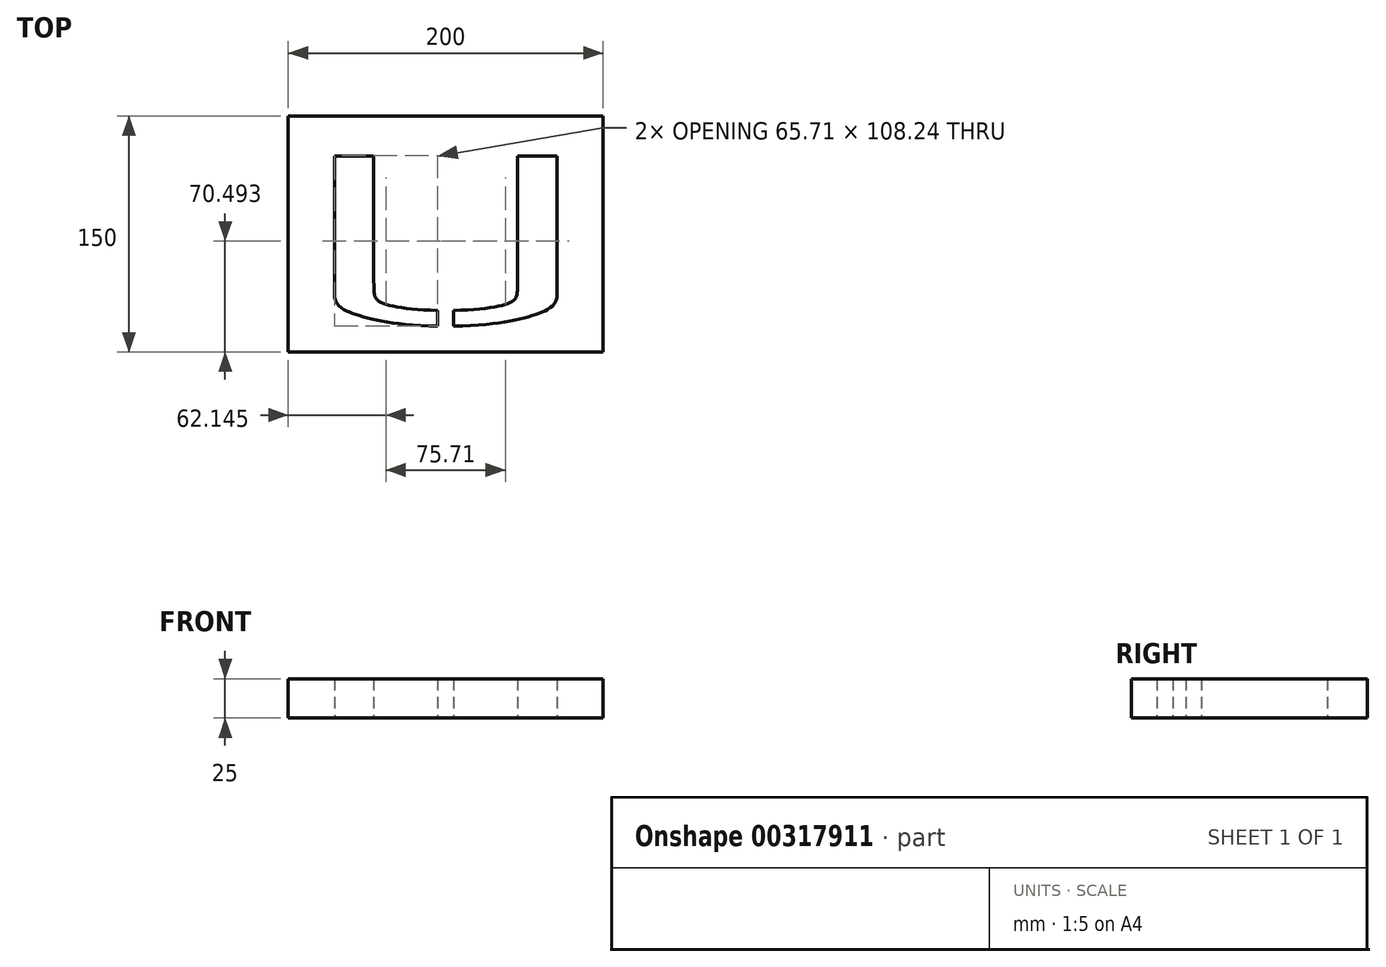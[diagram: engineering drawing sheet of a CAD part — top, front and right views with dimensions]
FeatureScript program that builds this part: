
annotation { "Feature Type Name" : "Feature", "Feature Type Description" : "" }
export const myFeature = defineFeature(function(context is Context, id is Id, definition is map)
    precondition{}
    {
        {
            var Q0;
            Q0=qCreatedBy(makeId("Top.planeOp"),FACE);
            var sketch = newSketch(context, id + "F0", { "sketchPlane" : qUnion([Q0])});
            skLineSegment(sketch, "E0.top", {"start": v(-40.71, 67.88) * mm, "end": v(-65.71, 67.88) * mm});
            skLineSegment(sketch, "E0.left", {"start": v(-40.71, -12.12) * mm, "end": v(-40.71, 67.88) * mm});
            skLineSegment(sketch, "E0.right", {"start": v(-65.71, -22.12) * mm, "end": v(-65.71, 67.88) * mm});
            skPoint(sketch, "E0.middle", {"position": v(-53.21, 22.88) * mm});
            skFitSpline(sketch, "E1", {"points": [v(-65.71, -22.12) * mm, v(-54.24, -32.12) * mm, v(0, -40.36) * mm], "startDerivative": vector(13.25, -51.58) * mm, "endDerivative": vector(134.92, -3.83) * mm});
            skFitSpline(sketch, "E2", {"points": [v(-40.71, -12.12) * mm, v(-39.12, -22.97) * mm, v(0, -30.36) * mm], "startDerivative": vector(2.76, -53.1) * mm, "endDerivative": vector(110.12, -4.2) * mm});
            skLineSegment(sketch, "E3", {"start": v(0, -30.36) * mm, "end": v(0, -40.36) * mm});
            skFitSpline(sketch, "E4.MirrorCS", {"points": [v(75.71, -22.12) * mm, v(64.24, -32.12) * mm, v(10, -40.36) * mm], "startDerivative": vector(-13.25, -51.58) * mm, "endDerivative": vector(-134.92, -3.83) * mm});
            skPoint(sketch, "E5.MirrorP", {"position": v(63.21, 22.88) * mm});
            skLineSegment(sketch, "E6.MirrorCS", {"start": v(50.71, -12.12) * mm, "end": v(50.71, 67.88) * mm});
            skLineSegment(sketch, "E7.MirrorCS", {"start": v(75.71, -22.12) * mm, "end": v(75.71, 67.88) * mm});
            skFitSpline(sketch, "E8.MirrorCS", {"points": [v(50.71, -12.12) * mm, v(49.12, -22.97) * mm, v(10, -30.36) * mm], "startDerivative": vector(-2.76, -53.1) * mm, "endDerivative": vector(-110.12, -4.2) * mm});
            skLineSegment(sketch, "E9.MirrorCS", {"start": v(10, -30.36) * mm, "end": v(10, -40.36) * mm});
            skLineSegment(sketch, "E10.MirrorCS", {"start": v(50.71, 67.88) * mm, "end": v(75.71, 67.88) * mm});
            skPoint(sketch, "E11.middle", {"position": v(0, 0) * mm});
            skLineSegment(sketch, "E12.bottom", {"start": v(-95, 93.27) * mm, "end": v(105, 93.27) * mm});
            skLineSegment(sketch, "E12.top", {"start": v(-95, -56.73) * mm, "end": v(105, -56.73) * mm});
            skLineSegment(sketch, "E12.left", {"start": v(-95, 93.27) * mm, "end": v(-95, -56.73) * mm});
            skLineSegment(sketch, "E12.right", {"start": v(105, 93.27) * mm, "end": v(105, -56.73) * mm});
            skLineSegment(sketch, "E13", {"start": v(0, 0) * mm, "end": v(5, 0) * mm});
            skPoint(sketch, "E14", {"position": v(5, -56.73) * mm});
            skSolve(sketch);
        }
        {
            var Q0;
            Q0=makeQuery(id+"F0.imprint","IMPRINT",FACE,{"disambiguationData":[TD([[makeQuery(id+"F0.imprint","IMPRINT",EDGE,{"derivedFrom":sQuery(id+"F0.wireOp",EDGE,"E0.top")}),-1.0]])]});
            extrude(context, id + "F1", {"entities" : qUnion([Q0]), "depth" : 25 * mm});
        }
    });
